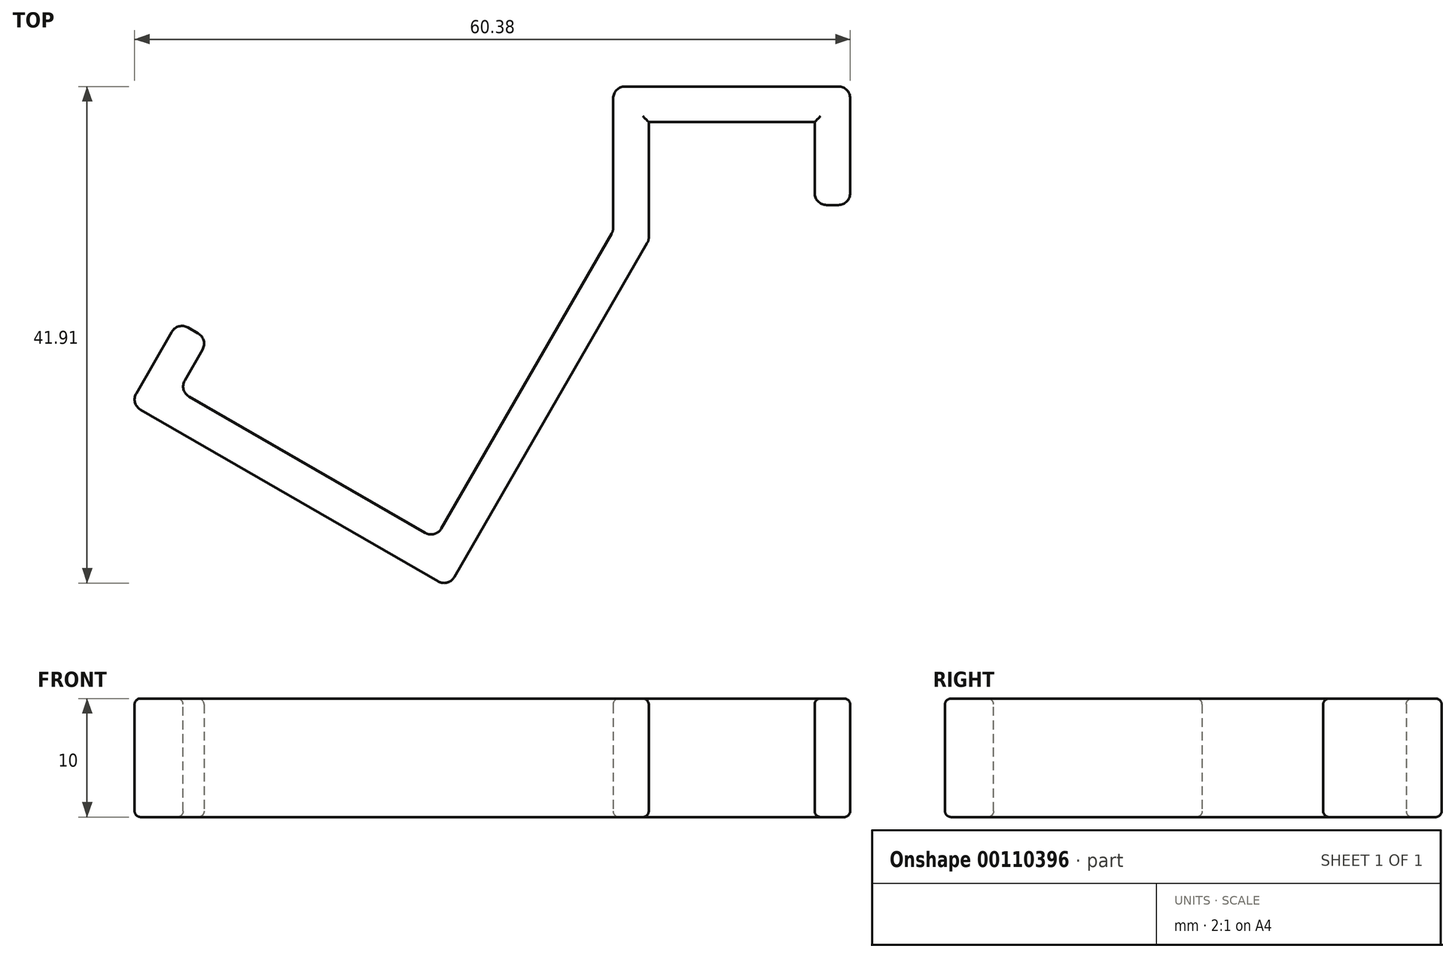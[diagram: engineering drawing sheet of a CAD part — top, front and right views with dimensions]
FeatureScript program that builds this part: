
annotation { "Feature Type Name" : "Feature", "Feature Type Description" : "" }
export const myFeature = defineFeature(function(context is Context, id is Id, definition is map)
    precondition{}
    {
        {
            var Q0;
            Q0=qCreatedBy(makeId("Top.planeOp"),FACE);
            var sketch = newSketch(context, id + "F0", { "sketchPlane" : qUnion([Q0])});
            skLineSegment(sketch, "E0", {"start": v(0, 0) * mm, "end": v(0, 7) * mm});
            skLineSegment(sketch, "E1", {"start": v(0, 7) * mm, "end": v(-14, 7) * mm});
            skLineSegment(sketch, "E2", {"start": v(-14, 7) * mm, "end": v(-14, -3) * mm});
            skLineSegment(sketch, "E3", {"start": v(-14, -3) * mm, "end": v(-30.9, -32.27) * mm});
            skLineSegment(sketch, "E4", {"start": v(-30.9, -32.27) * mm, "end": v(-57.75, -16.77) * mm});
            skLineSegment(sketch, "E5", {"start": v(-57.75, -16.77) * mm, "end": v(-53.75, -9.85) * mm});
            skLineSegment(sketch, "E6", {"start": v(-53.75, -9.85) * mm, "end": v(-51.15, -11.35) * mm});
            skLineSegment(sketch, "E7", {"start": v(-51.15, -11.35) * mm, "end": v(-53.65, -15.68) * mm});
            skLineSegment(sketch, "E8", {"start": v(-53.65, -15.68) * mm, "end": v(-32, -28.18) * mm});
            skLineSegment(sketch, "E9", {"start": v(-32, -28.18) * mm, "end": v(-17, -2.2) * mm});
            skLineSegment(sketch, "E10", {"start": v(-17, -2.2) * mm, "end": v(-17, 10) * mm});
            skLineSegment(sketch, "E11", {"start": v(-17, 10) * mm, "end": v(3, 10) * mm});
            skLineSegment(sketch, "E12", {"start": v(3, 10) * mm, "end": v(3, 0) * mm});
            skLineSegment(sketch, "E13", {"start": v(3, 0) * mm, "end": v(0, 0) * mm});
            skSolve(sketch);
        }
        {
            var Q0;
            Q0 = qSketchRegion(id + "F0", true);
            extrude(context, id + "F1", {"entities" : qUnion([Q0]), "depth" : 10 * mm, "offsetDistance" : 25 * mm});
        }
        {
            var Q0;
            Q0=makeQuery(id+"F1.opExtrude","SWEPT_EDGE",EDGE,{"disambiguationData":[OSD([sQuery(id+"F0.wireOp",EDGE,"E10"),sQuery(id+"F0.wireOp",EDGE,"E11")])]});
            var Q1;
            Q1=makeQuery(id+"F1.opExtrude","SWEPT_EDGE",EDGE,{"disambiguationData":[OSD([sQuery(id+"F0.wireOp",EDGE,"E11"),sQuery(id+"F0.wireOp",EDGE,"E12")])]});
            var Q2;
            Q2=makeQuery(id+"F1.opExtrude","SWEPT_EDGE",EDGE,{"disambiguationData":[OSD([sQuery(id+"F0.wireOp",EDGE,"E9"),sQuery(id+"F0.wireOp",EDGE,"E10")])]});
            var Q3;
            Q3=makeQuery(id+"F1.opExtrude","SWEPT_EDGE",EDGE,{"disambiguationData":[OSD([sQuery(id+"F0.wireOp",EDGE,"E2"),sQuery(id+"F0.wireOp",EDGE,"E3")])]});
            var Q4;
            Q4=makeQuery(id+"F1.opExtrude","SWEPT_EDGE",EDGE,{"disambiguationData":[OSD([sQuery(id+"F0.wireOp",EDGE,"E12"),sQuery(id+"F0.wireOp",EDGE,"E13")])]});
            var Q5;
            Q5=makeQuery(id+"F1.opExtrude","SWEPT_EDGE",EDGE,{"disambiguationData":[OSD([sQuery(id+"F0.wireOp",EDGE,"E0"),sQuery(id+"F0.wireOp",EDGE,"E13")])]});
            var Q6;
            Q6=makeQuery(id+"F1.opExtrude","SWEPT_EDGE",EDGE,{"disambiguationData":[OSD([sQuery(id+"F0.wireOp",EDGE,"E3"),sQuery(id+"F0.wireOp",EDGE,"E4")])]});
            var Q7;
            Q7=makeQuery(id+"F1.opExtrude","SWEPT_EDGE",EDGE,{"disambiguationData":[OSD([sQuery(id+"F0.wireOp",EDGE,"E8"),sQuery(id+"F0.wireOp",EDGE,"E9")])]});
            var Q8;
            Q8=makeQuery(id+"F1.opExtrude","SWEPT_EDGE",EDGE,{"disambiguationData":[OSD([sQuery(id+"F0.wireOp",EDGE,"E7"),sQuery(id+"F0.wireOp",EDGE,"E8")])]});
            var Q9;
            Q9=makeQuery(id+"F1.opExtrude","SWEPT_EDGE",EDGE,{"disambiguationData":[OSD([sQuery(id+"F0.wireOp",EDGE,"E6"),sQuery(id+"F0.wireOp",EDGE,"E7")])]});
            var Q10;
            Q10=makeQuery(id+"F1.opExtrude","SWEPT_EDGE",EDGE,{"disambiguationData":[OSD([sQuery(id+"F0.wireOp",EDGE,"E5"),sQuery(id+"F0.wireOp",EDGE,"E6")])]});
            var Q11;
            Q11=makeQuery(id+"F1.opExtrude","SWEPT_EDGE",EDGE,{"disambiguationData":[OSD([sQuery(id+"F0.wireOp",EDGE,"E4"),sQuery(id+"F0.wireOp",EDGE,"E5")])]});
            fillet(context, id + "F2", {"entities" : qUnion([Q0, Q1, Q2, Q3, Q4, Q5, Q6, Q7, Q8, Q9, Q10, Q11]), "radius" : 1 * mm, "tangentPropagation" : true, "allowEdgeOverflow" : false});
        }
        {
            var Q0;
            Q0=makeQuery(id+"F1.opExtrude","CAP_EDGE",EDGE,{"disambiguationData":[OSD([sQuery(id+"F0.wireOp",EDGE,"E3")])],"isStart":false});
            var Q1;
            Q1=makeQuery(id+"F1.opExtrude","CAP_EDGE",EDGE,{"disambiguationData":[OSD([sQuery(id+"F0.wireOp",EDGE,"E1")])],"isStart":false});
            var Q2;
            Q2=makeQuery(id+"F1.opExtrude","CAP_EDGE",EDGE,{"disambiguationData":[OSD([sQuery(id+"F0.wireOp",EDGE,"E3")])],"isStart":true});
            var Q3;
            Q3=makeQuery(id+"F1.opExtrude","CAP_EDGE",EDGE,{"disambiguationData":[OSD([sQuery(id+"F0.wireOp",EDGE,"E1")])],"isStart":true});
            fillet(context, id + "F3", {"entities" : qUnion([Q0, Q1, Q2, Q3]), "radius" : 0.5 * mm, "tangentPropagation" : true, "allowEdgeOverflow" : false});
        }
    });
